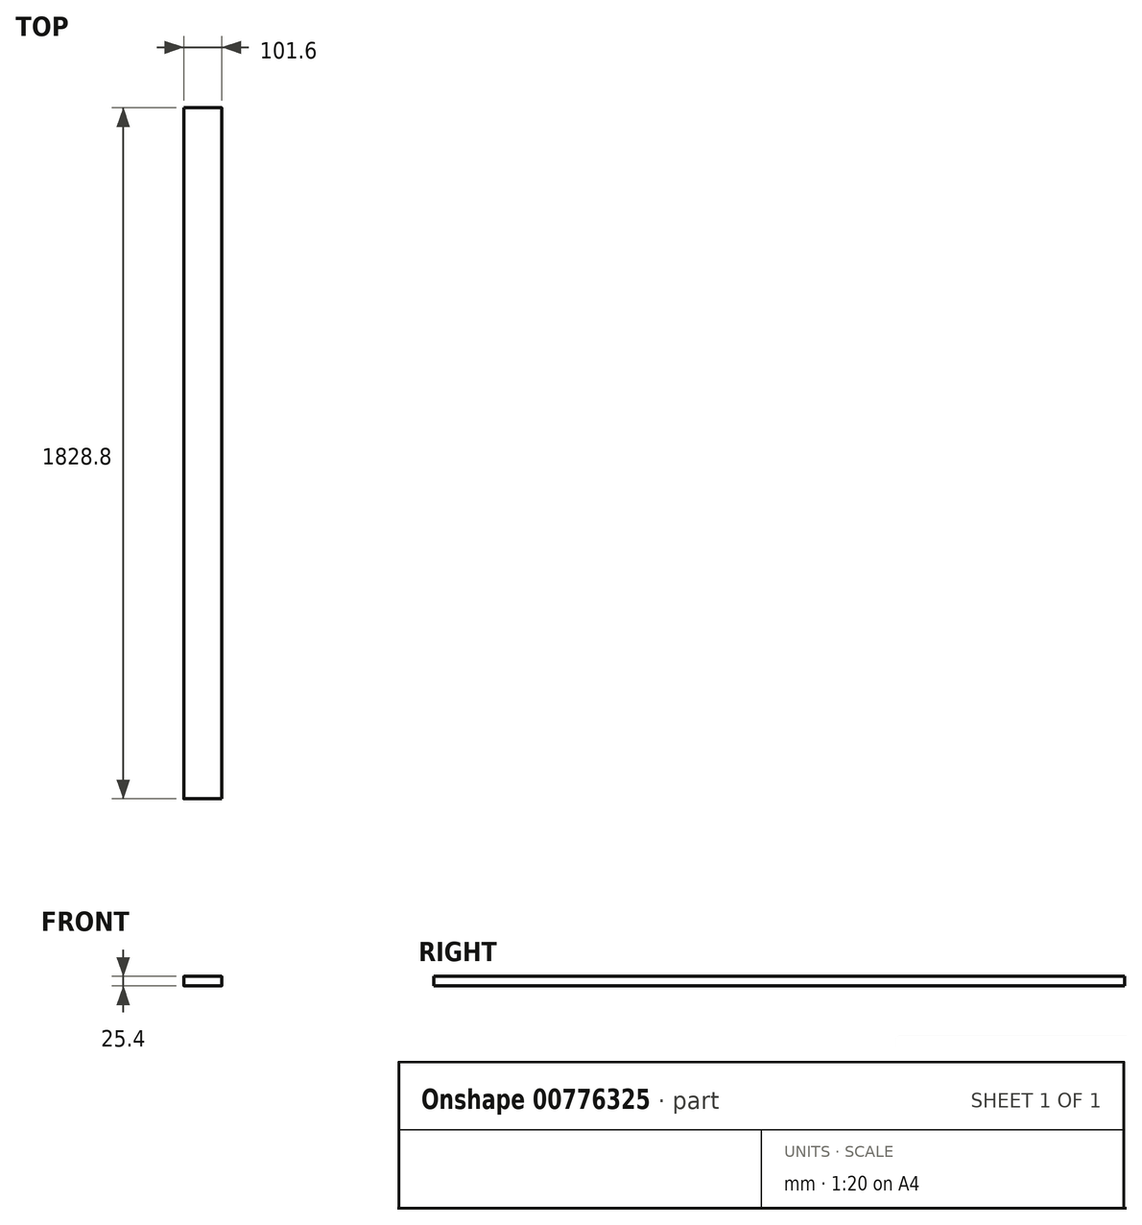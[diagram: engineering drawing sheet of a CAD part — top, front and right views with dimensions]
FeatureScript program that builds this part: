
annotation { "Feature Type Name" : "Feature", "Feature Type Description" : "" }
export const myFeature = defineFeature(function(context is Context, id is Id, definition is map)
    precondition{}
    {
        {
            var Q0;
            Q0=qCreatedBy(makeId("Top.planeOp"),FACE);
            var sketch = newSketch(context, id + "F0", { "sketchPlane" : qUnion([Q0])});
            skLineSegment(sketch, "E0.bottom", {"start": v(50.8, 914.4) * mm, "end": v(-50.8, 914.4) * mm});
            skLineSegment(sketch, "E0.top", {"start": v(50.8, -914.4) * mm, "end": v(-50.8, -914.4) * mm});
            skLineSegment(sketch, "E0.left", {"start": v(50.8, 914.4) * mm, "end": v(50.8, -914.4) * mm});
            skLineSegment(sketch, "E0.right", {"start": v(-50.8, 914.4) * mm, "end": v(-50.8, -914.4) * mm});
            skPoint(sketch, "E0.middle", {"position": v(0, 0) * mm});
            skSolve(sketch);
        }
        {
            var Q0;
            Q0=makeQuery(id+"F0.imprint","IMPRINT",FACE,{"disambiguationData":[TD([[makeQuery(id+"F0.imprint","IMPRINT",EDGE,{"derivedFrom":sQuery(id+"F0.wireOp",EDGE,"E0.bottom")}),1.0]])]});
            extrude(context, id + "F1", {"entities" : qUnion([Q0]), "endBound" : BoundingType.SYMMETRIC, "depth" : 25.4 * mm, "offsetDistance" : 25.4 * mm});
        }
        {
            var Q0;
            Q0=makeQuery(id+"F1.opExtrude","CAP_EDGE",EDGE,{"disambiguationData":[OSD([sQuery(id+"F0.wireOp",EDGE,"E0.left")])],"isStart":false});
            var Q1;
            Q1=makeQuery(id+"F1.opExtrude","CAP_EDGE",EDGE,{"disambiguationData":[OSD([sQuery(id+"F0.wireOp",EDGE,"E0.right")])],"isStart":false});
            var Q2;
            Q2=makeQuery(id+"F1.opExtrude","CAP_EDGE",EDGE,{"disambiguationData":[OSD([sQuery(id+"F0.wireOp",EDGE,"E0.left")])],"isStart":true});
            var Q3;
            Q3=makeQuery(id+"F1.opExtrude","CAP_EDGE",EDGE,{"disambiguationData":[OSD([sQuery(id+"F0.wireOp",EDGE,"E0.right")])],"isStart":true});
            fillet(context, id + "F2", {"entities" : qUnion([Q0, Q1, Q2, Q3]), "radius" : 1.59 * mm, "tangentPropagation" : true, "allowEdgeOverflow" : false});
        }
    });
